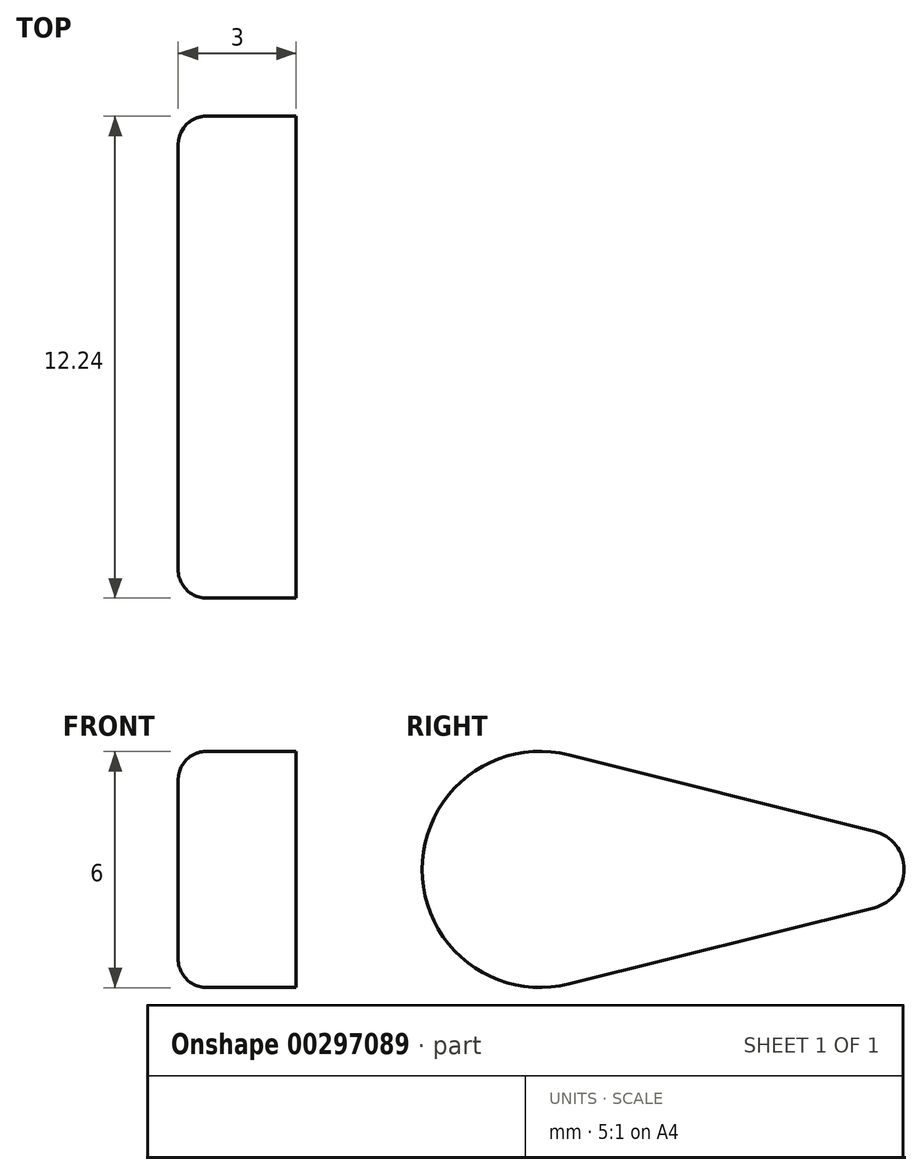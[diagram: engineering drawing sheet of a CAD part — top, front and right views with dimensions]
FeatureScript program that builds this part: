
annotation { "Feature Type Name" : "Feature", "Feature Type Description" : "" }
export const myFeature = defineFeature(function(context is Context, id is Id, definition is map)
    precondition{}
    {
        {
            var Q0;
            Q0=qCreatedBy(makeId("Right.planeOp"),FACE);
            var sketch = newSketch(context, id + "F0", { "sketchPlane" : qUnion([Q0])});
            skCircle(sketch, "E0", {"center": v(15.89, 17.25) * mm, "radius": 3 * mm});
            skCircle(sketch, "E1", {"center": v(24.13, 17.25) * mm, "radius": 1 * mm});
            skLineSegment(sketch, "E2", {"start": v(16.61, 20.16) * mm, "end": v(24.38, 18.22) * mm});
            skLineSegment(sketch, "E3", {"start": v(16.61, 14.34) * mm, "end": v(24.38, 16.28) * mm});
            skSolve(sketch);
        }
        {
            var Q0;
            {var subQ0=sQuery(id+"F0.wireOp",EDGE,"E0");var subQ1=makeQuery(id+"F0.imprint","INTERSECT",VERTEX,{"derivedFrom":[subQ0,sQuery(id+"F0.wireOp",EDGE,"E2")]});Q0=makeQuery(id+"F0.imprint","IMPRINT",FACE,{"disambiguationData":[TD([[makeQuery(id+"F0.imprint","IMPRINT",EDGE,{"disambiguationData":[TD([[subQ1,-1.0]])],"derivedFrom":subQ0}),1.0]])]});}
            var Q1;
            {var subQ0=sQuery(id+"F0.wireOp",EDGE,"E2");Q1=makeQuery(id+"F0.imprint","IMPRINT",FACE,{"disambiguationData":[TD([[makeQuery(id+"F0.imprint","IMPRINT",EDGE,{"derivedFrom":subQ0}),-1.0]])]});}
            var Q2;
            {var subQ0=sQuery(id+"F0.wireOp",EDGE,"E1");var subQ1=makeQuery(id+"F0.imprint","INTERSECT",VERTEX,{"derivedFrom":[subQ0,sQuery(id+"F0.wireOp",EDGE,"E2")]});Q2=makeQuery(id+"F0.imprint","IMPRINT",FACE,{"disambiguationData":[TD([[makeQuery(id+"F0.imprint","IMPRINT",EDGE,{"disambiguationData":[TD([[subQ1,-1.0]])],"derivedFrom":subQ0}),1.0]])]});}
            extrude(context, id + "F1", {"entities" : qUnion([Q0, Q1, Q2]), "depth" : 3 * mm});
        }
        {
            var Q0;
            Q0=makeQuery(id+"F1.opExtrude","CAP_EDGE",EDGE,{"disambiguationData":[OSD([sQuery(id+"F0.wireOp",EDGE,"E2")])],"isStart":true});
            fillet(context, id + "F2", {"entities" : qUnion([Q0]), "radius" : 0.72 * mm, "tangentPropagation" : true, "allowEdgeOverflow" : false});
        }
    });
